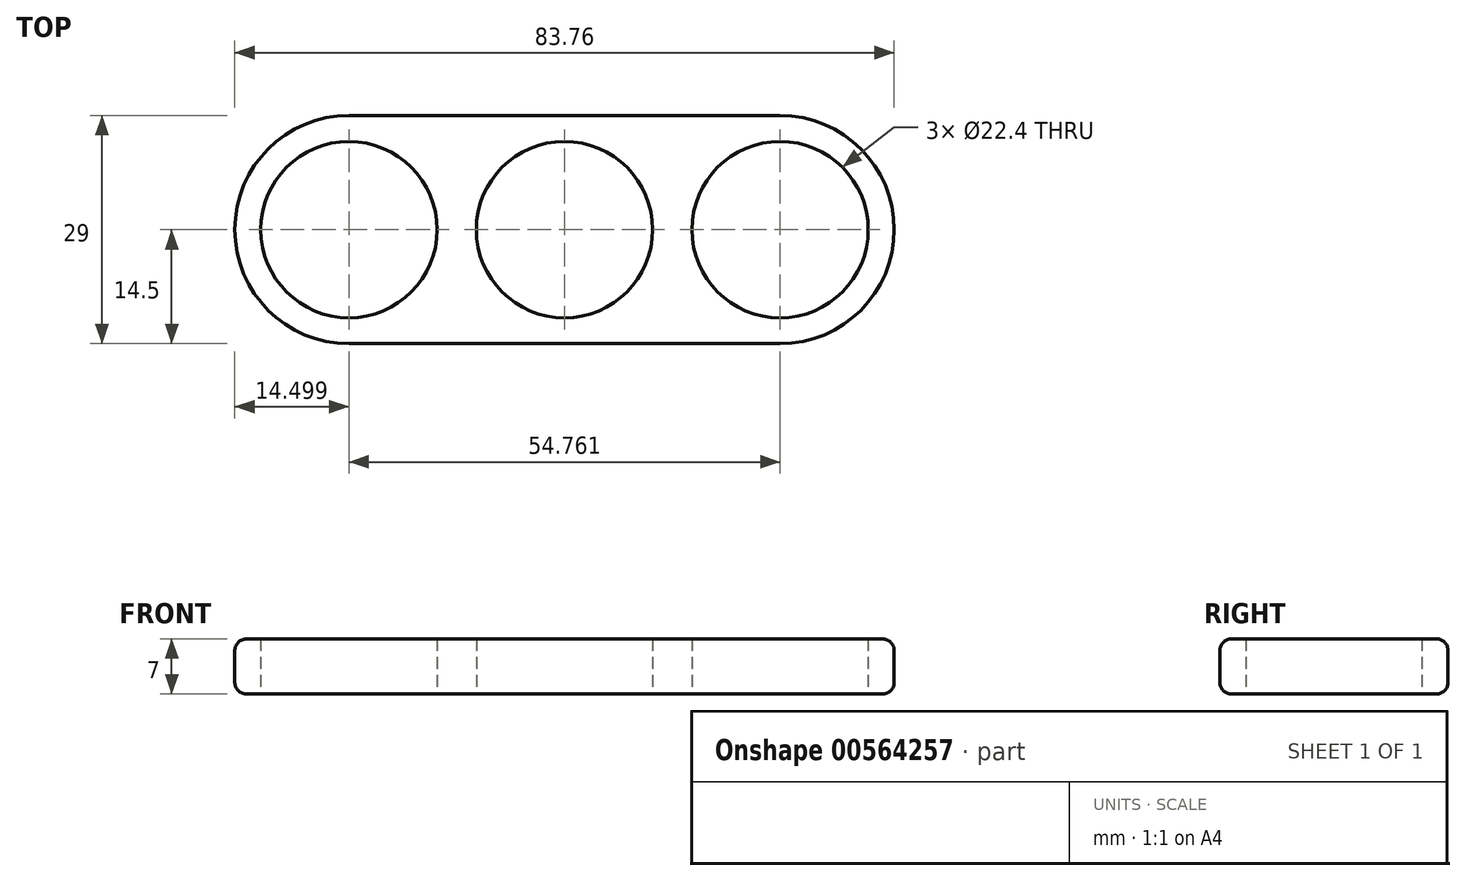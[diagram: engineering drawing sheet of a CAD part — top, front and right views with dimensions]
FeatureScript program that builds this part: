
annotation { "Feature Type Name" : "Feature", "Feature Type Description" : "" }
export const myFeature = defineFeature(function(context is Context, id is Id, definition is map)
    precondition{}
    {
        {
            var Q0;
            Q0=qCreatedBy(makeId("Top.planeOp"),FACE);
            var sketch = newSketch(context, id + "F0", { "sketchPlane" : qUnion([Q0])});
            skCircle(sketch, "E0", {"center": v(0, 0) * mm, "radius": 11.2 * mm});
            skCircle(sketch, "E1", {"center": v(27.38, 0) * mm, "radius": 11.2 * mm});
            skArc(sketch, "E2", {"start": v(27.38, -14.5) * mm, "mid": v(41.88, 0) * mm, "end": v(27.38, 14.5) * mm});
            skCircle(sketch, "E3.1.0", {"center": v(-27.38, 0) * mm, "radius": 11.2 * mm});
            skArc(sketch, "E4.1.0", {"start": v(-27.38, 14.5) * mm, "mid": v(-41.88, 0) * mm, "end": v(-27.38, -14.5) * mm});
            skLineSegment(sketch, "E5", {"start": v(-27.38, 14.5) * mm, "end": v(27.38, 14.5) * mm});
            skLineSegment(sketch, "E6", {"start": v(27.38, -14.5) * mm, "end": v(-27.38, -14.5) * mm});
            skSolve(sketch);
        }
        {
            var Q0;
            Q0=makeQuery(id+"F0.imprint","IMPRINT",FACE,{"disambiguationData":[TD([[makeQuery(id+"F0.imprint","IMPRINT",EDGE,{"derivedFrom":sQuery(id+"F0.wireOp",EDGE,"E0")}),-1.0]])]});
            extrude(context, id + "F1", {"entities" : qUnion([Q0]), "depth" : 7 * mm, "offsetDistance" : 25 * mm});
        }
        {
            var Q0;
            Q0=makeQuery(id+"F1.opExtrude","CAP_EDGE",EDGE,{"disambiguationData":[OSD([sQuery(id+"F0.wireOp",EDGE,"E6")])],"isStart":false});
            var Q1;
            Q1=makeQuery(id+"F1.opExtrude","CAP_EDGE",EDGE,{"disambiguationData":[OSD([sQuery(id+"F0.wireOp",EDGE,"E6")])],"isStart":true});
            fillet(context, id + "F2", {"entities" : qUnion([Q0, Q1]), "radius" : 1.5 * mm, "tangentPropagation" : true, "allowEdgeOverflow" : false});
        }
    });
